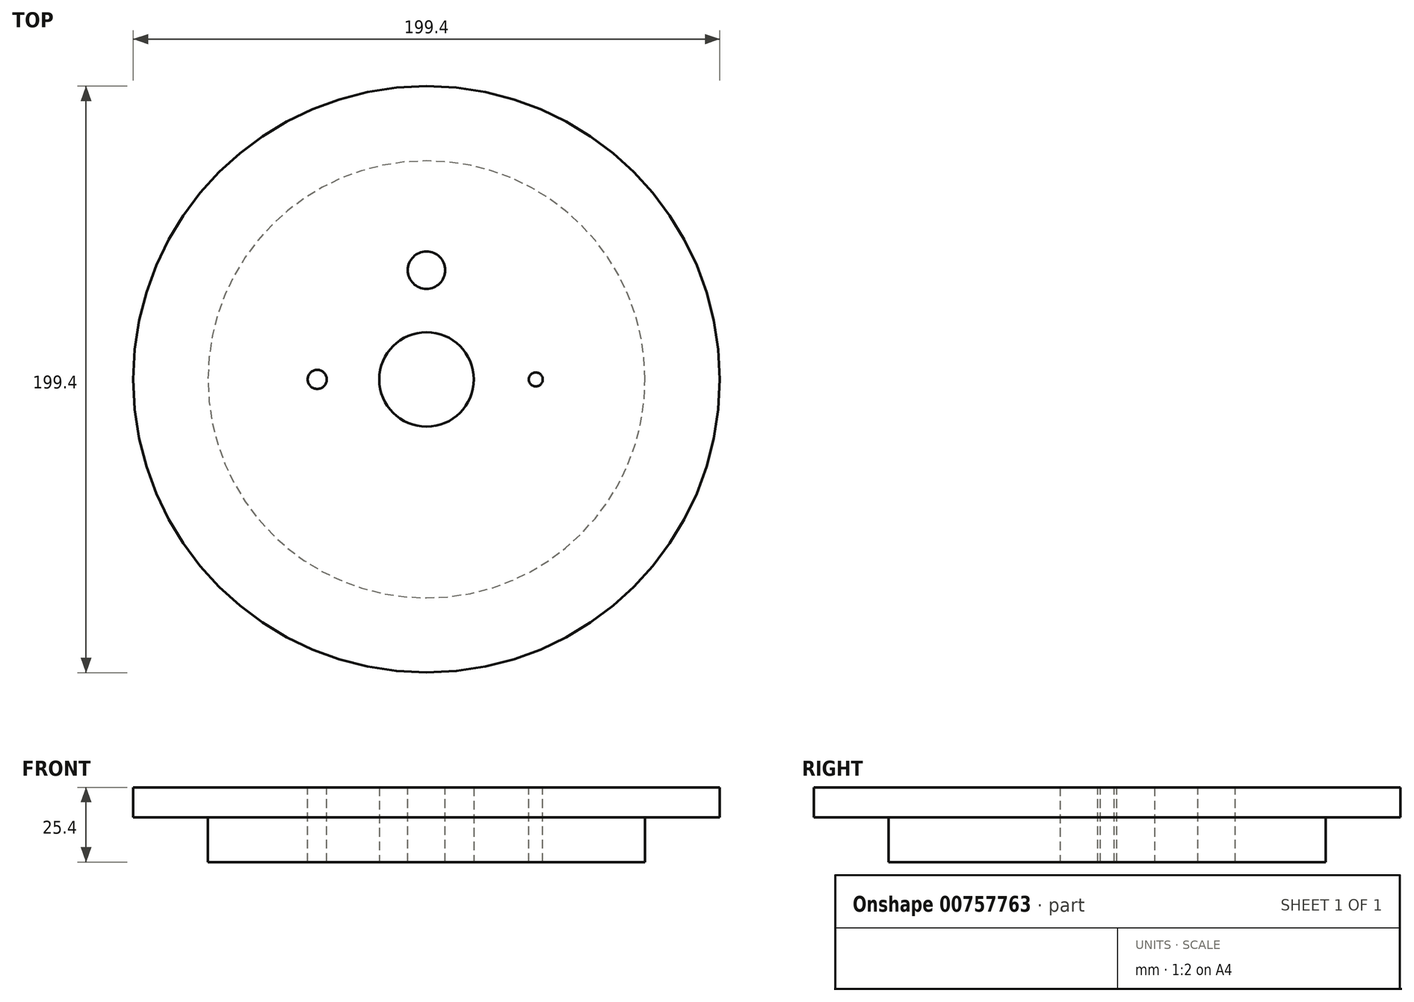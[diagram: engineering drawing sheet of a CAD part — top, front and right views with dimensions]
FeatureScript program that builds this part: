
annotation { "Feature Type Name" : "Feature", "Feature Type Description" : "" }
export const myFeature = defineFeature(function(context is Context, id is Id, definition is map)
    precondition{}
    {
        {
            var Q0;
            Q0=qCreatedBy(makeId("Front.planeOp"),FACE);
            var sketch = newSketch(context, id + "F0", { "sketchPlane" : qUnion([Q0])});
            skLineSegment(sketch, "E0.bottom", {"start": v(16.07, -12.7) * mm, "end": v(99.7, -12.7) * mm});
            skLineSegment(sketch, "E0.top", {"start": v(16.07, 12.7) * mm, "end": v(99.7, 12.7) * mm});
            skLineSegment(sketch, "E0.left", {"start": v(0, -12.7) * mm, "end": v(0, 12.7) * mm, "construction": true});
            skLineSegment(sketch, "E0.right", {"start": v(99.7, -12.7) * mm, "end": v(99.7, 12.7) * mm});
            skPoint(sketch, "E1", {"position": v(16.07, -12.7) * mm});
            skLineSegment(sketch, "E2", {"start": v(16.07, -12.7) * mm, "end": v(16.07, 12.7) * mm});
            skLineSegment(sketch, "E3", {"start": v(2.67, 0) * mm, "end": v(13.37, 0) * mm, "construction": true});
            skSolve(sketch);
        }
        {
            var Q0;
            Q0 = qSketchRegion(id + "F0", true);
            var Q1;
            Q1=sQuery(id+"F0.wireOp",EDGE,"E0.left");
            revolve(context, id + "F1", {"surfaceOperationType" : NewSurfaceOperationType.NEW, "entities" : qUnion([Q0]), "axis" : qUnion([Q1]), "revolveType" : RevolveType.FULL});
        }
        {
            var Q0;
            Q0=qCreatedBy(makeId("Top.planeOp"),FACE);
            var sketch = newSketch(context, id + "F2", { "sketchPlane" : qUnion([Q0])});
            skPoint(sketch, "E4", {"position": v(37.15, 0) * mm});
            skCircle(sketch, "E5", {"center": v(37.15, 0) * mm, "radius": 2.38 * mm});
            skPoint(sketch, "E6", {"position": v(-37.15, 0) * mm});
            skPoint(sketch, "E7", {"position": v(0, 37.15) * mm});
            skCircle(sketch, "E8", {"center": v(-37.15, 0) * mm, "radius": 3.24 * mm});
            skCircle(sketch, "E9", {"center": v(0, 37.15) * mm, "radius": 6.35 * mm});
            skSolve(sketch);
        }
        {
            var Q0;
            Q0 = qSketchRegion(id + "F2", true);
            extrude(context, id + "F3", {"entities" : qUnion([Q0]), "operationType" : NewBodyOperationType.REMOVE, "endBound" : BoundingType.THROUGH_ALL, "oppositeDirection" : true, "depth" : 25.4 * mm, "offsetDistance" : 25.4 * mm, "hasSecondDirection" : true, "secondDirectionBound" : SecondDirectionBoundingType.THROUGH_ALL, "secondDirectionOppositeDirection" : false, "secondDirectionDepth" : 25.4 * mm});
        }
        {
            var Q0;
            Q0=qCreatedBy(makeId("Front.planeOp"),FACE);
            var sketch = newSketch(context, id + "F4", { "sketchPlane" : qUnion([Q0])});
            skLineSegment(sketch, "E10.bottom", {"start": v(99.7, 2.54) * mm, "end": v(74.3, 2.54) * mm});
            skLineSegment(sketch, "E10.top", {"start": v(99.7, -12.7) * mm, "end": v(74.3, -12.7) * mm});
            skLineSegment(sketch, "E10.left", {"start": v(99.7, 2.54) * mm, "end": v(99.7, -12.7) * mm});
            skLineSegment(sketch, "E10.right", {"start": v(74.3, 2.54) * mm, "end": v(74.3, -12.7) * mm});
            skLineSegment(sketch, "E11", {"start": v(0, 9.65) * mm, "end": v(0, -8.49) * mm, "construction": true});
            skSolve(sketch);
        }
        {
            var Q0;
            Q0 = qSketchRegion(id + "F4", true);
            var Q1;
            Q1=sQuery(id+"F4.wireOp",EDGE,"E11");
            revolve(context, id + "F5", {"operationType" : NewBodyOperationType.REMOVE, "surfaceOperationType" : NewSurfaceOperationType.NEW, "entities" : qUnion([Q0]), "axis" : qUnion([Q1]), "revolveType" : RevolveType.FULL, "oppositeDirection" : true});
        }
    });
